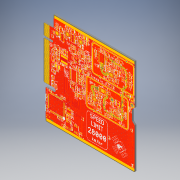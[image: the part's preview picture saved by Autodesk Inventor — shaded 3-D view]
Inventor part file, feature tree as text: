
AUTODESK INVENTOR PART (.ipt)
format: ipt  version: 2018 (Build 220112000, 112)  size: 3,501,568 bytes
history: native  units: in
note: dims shown in document units (in); Inventor stores cm internally (conversion verified against a paired STEP export)
features: sketch x8, other x4, hole x4, projected_geometry x3, extrude x2, fillet x2, chamfer x1
ambient origin geometry x8: Origin, YZ Plane, XZ Plane, XY Plane, X Axis, Y Axis, Z Axis, Center Point
bodies: Solid1 (feature_tree)
feature tree (24):
  extrude  "Extrusion1"  Depth=3.7717in
  chamfer  "Chamfer1"  Distance=0.063in
  fillet  "Fillet1"  Radius=3.7795in
  extrude  "Extrusion6"  Depth=0.0039in
  fillet  "Fillet2"  Radius=0.0039in
  other  "Decal5"
  other  "Decal6"
  hole  "Hole13"  [1 undecoded]
  hole  "Hole14"  [1 undecoded]
  hole  "Hole15"  [1 undecoded]
  hole  "Hole16"  [1 undecoded]
  sketch  "Sketch29"  dims[d36=1.5413in d37=0.5709in d38=0.0453in d39=0.0709in d40=2.7559in d42=0.0709in d43=1.9685in d45=0.0709in d48=0.0787in d49=0.1339in d50=0.0748in d51=0.3307in d52=0.9449in d53=0.0197in d54=0.0787in d55=45.0deg d56=0.0197in d145=0.0984in d146=0.3937in d147=0.3937in d148=0.0in d149=0.0394in d193=0.0866in d194=0.2362in d195=0.1575in d196=0.0787in d197=90.0deg d198=0.315in d199=0.8108in d200=0.0472in d201=0.2362in d202=0.1575in d203=0.0787in d204=90.0deg d205=0.315in d206=0.8108in d207=0.0138in d208=0.2362in d209=0.1575in d210=0.0787in d211=90.0deg d212=0.315in d213=0.8108in d214=0.0118in d215=0.2362in d216=0.1575in d217=0.0787in d218=90.0deg d219=0.315in d220=0.8108in d221=0.0197in d222=0.1181in d223=0.7874in d225=0.0394in d226=9.8425in d228=0.0394in]
  sketch  "Sketch16"  dims[d0=2.0197in d1=3.7717in]
  projected_geometry  "Projected Loop5"
  sketch  "Sketch23"  dims[d3=0.3937in d4=0.063in d5=0.0in d20=3.7795in]
  other  "Image9"
  sketch  "Sketch24"  dims[d21=3.7795in d22=0.0039in d23=0.0039in]
  projected_geometry  "Projected Loop6"
  other  "Image10"
  sketch  "Sketch25"  dims[d24=0.0787in d25=0.0039in]
  sketch  "Sketch26"  dims[d28=0.4429in d29=2.2047in]
  sketch  "Sketch27"  dims[d31=0.374in d32=1.2008in]
  sketch  "Sketch28"  dims[d34=0.1378in d35=0.4783in]
  projected_geometry  "Projected Loop7"
note: 4 required parameter values undecoded (feature->parameter linkage not recoverable at this tier; creation-order binding heuristic only, values carry confidence <= 0.55)
